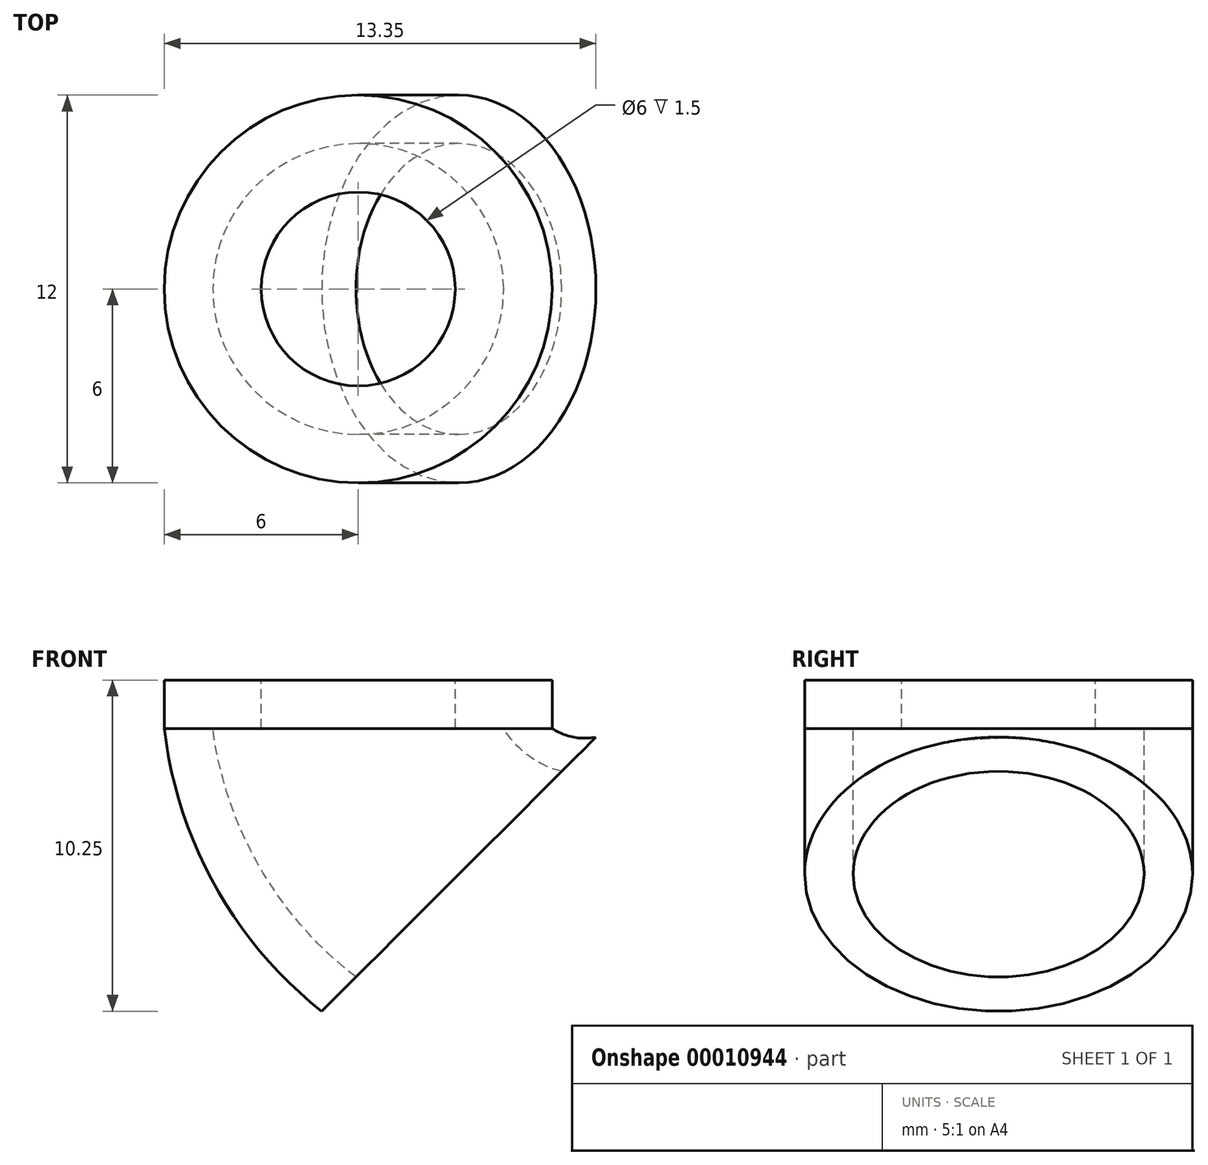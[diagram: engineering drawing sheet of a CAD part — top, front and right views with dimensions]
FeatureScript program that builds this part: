
annotation { "Feature Type Name" : "Feature", "Feature Type Description" : "" }
export const myFeature = defineFeature(function(context is Context, id is Id, definition is map)
    precondition{}
    {
        {
            var Q0;
            Q0=qCreatedBy(makeId("Top.planeOp"),FACE);
            var sketch = newSketch(context, id + "F0", { "sketchPlane" : qUnion([Q0])});
            skLineSegment(sketch, "E0", {"start": v(0, 0) * mm, "end": v(-80, 0) * mm, "construction": true});
            skCircle(sketch, "E1", {"center": v(-80, 0) * mm, "radius": 3 * mm});
            skCircle(sketch, "E2", {"center": v(-80, 0) * mm, "radius": 4.5 * mm});
            skCircle(sketch, "E3", {"center": v(-80, 0) * mm, "radius": 6 * mm});
            skLineSegment(sketch, "E4", {"start": v(-73, 0) * mm, "end": v(-73, 5) * mm, "construction": true});
            skSolve(sketch);
        }
        {
            var Q0;
            Q0=makeQuery(id+"F0.imprint","IMPRINT",FACE,{"disambiguationData":[TD([[makeQuery(id+"F0.imprint","IMPRINT",EDGE,{"derivedFrom":sQuery(id+"F0.wireOp",EDGE,"E2")}),-1.0]])]});
            extrude(context, id + "F1", {"entities" : qUnion([Q0]), "oppositeDirection" : true, "depth" : 1.5 * mm});
        }
        {
            var Q0;
            Q0=makeQuery(id+"F1.opExtrude","CAP_FACE",FACE,{"disambiguationData":[OSD([sQuery(id+"F0.wireOp",EDGE,"E2"),sQuery(id+"F0.wireOp",EDGE,"E3")])],"isStart":false});
            var Q1;
            Q1=sQuery(id+"F0.wireOp",EDGE,"E4");
            revolve(context, id + "F2", {"operationType" : NewBodyOperationType.ADD, "entities" : qUnion([Q0]), "axis" : qUnion([Q1]), "revolveType" : RevolveType.ONE_DIRECTION, "oppositeDirection" : true, "angle" : 45 * degree});
        }
        {
            var Q0;
            Q0=makeQuery(id+"F0.imprint","IMPRINT",FACE,{"disambiguationData":[TD([[makeQuery(id+"F0.imprint","IMPRINT",EDGE,{"derivedFrom":sQuery(id+"F0.wireOp",EDGE,"E1")}),-1.0]])]});
            extrude(context, id + "F3", {"entities" : qUnion([Q0]), "operationType" : NewBodyOperationType.ADD, "oppositeDirection" : true, "depth" : 1.5 * mm});
        }
    });
